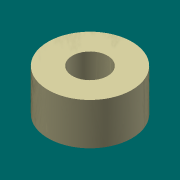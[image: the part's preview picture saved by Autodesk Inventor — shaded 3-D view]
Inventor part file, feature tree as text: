
AUTODESK INVENTOR PART (.ipt)
format: ipt  version: 2016 (Build 200138000, 138)  size: 95,232 bytes
history: native  units: mm
features: extrude x1
ambient origin geometry x8: Origin, YZ Plane, XZ Plane, XY Plane, X Axis, Y Axis, Z Axis, Center Point
bodies: Solid1 (feature_tree)
feature tree (1):
  extrude  "Extrude1"  [1 undecoded]
note: 1 required parameter value undecoded (feature->parameter linkage not recoverable at this tier; creation-order binding heuristic only, values carry confidence <= 0.55)
